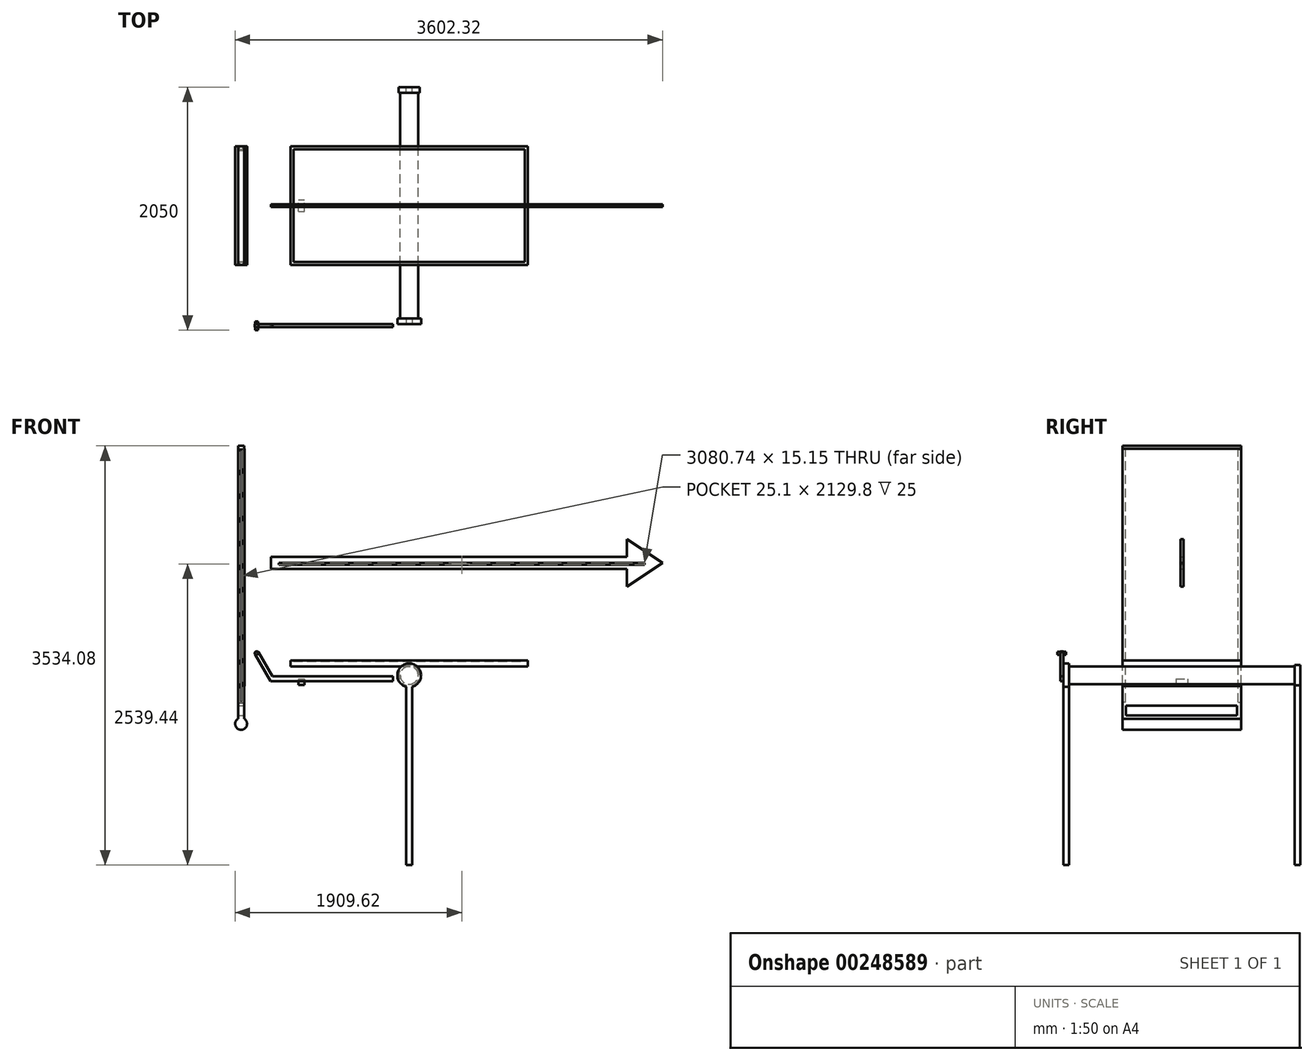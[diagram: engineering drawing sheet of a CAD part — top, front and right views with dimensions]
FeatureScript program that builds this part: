
annotation { "Feature Type Name" : "Feature", "Feature Type Description" : "" }
export const myFeature = defineFeature(function(context is Context, id is Id, definition is map)
    precondition{}
    {
        {
            var Q0;
            Q0=qCreatedBy(makeId("Top.planeOp"),FACE);
            var sketch = newSketch(context, id + "F0", { "sketchPlane" : qUnion([Q0])});
            skLineSegment(sketch, "E0.bottom", {"start": v(-1000, 500) * mm, "end": v(1000, 500) * mm});
            skLineSegment(sketch, "E0.top", {"start": v(-1000, -500) * mm, "end": v(1000, -500) * mm});
            skLineSegment(sketch, "E0.left", {"start": v(-1000, 500) * mm, "end": v(-1000, -500) * mm});
            skLineSegment(sketch, "E0.right", {"start": v(1000, 500) * mm, "end": v(1000, -500) * mm});
            skLineSegment(sketch, "E1", {"start": v(-1000, -500) * mm, "end": v(1000, 500) * mm, "construction": true});
            skSolve(sketch);
        }
        {
            var Q0;
            Q0=makeQuery(id+"F0.imprint","IMPRINT",FACE,{"disambiguationData":[TD([[makeQuery(id+"F0.imprint","IMPRINT",EDGE,{"derivedFrom":sQuery(id+"F0.wireOp",EDGE,"E0.bottom")}),-1.0]])]});
            extrude(context, id + "F1", {"entities" : qUnion([Q0]), "endBound" : BoundingType.SYMMETRIC, "depth" : 50 * mm});
        }
        {
            var Q0;
            Q0=makeQuery(id+"F1.opExtrude","CAP_FACE",FACE,{"disambiguationData":[OSD([sQuery(id+"F0.wireOp",EDGE,"E0.bottom"),sQuery(id+"F0.wireOp",EDGE,"E0.top"),sQuery(id+"F0.wireOp",EDGE,"E0.left"),sQuery(id+"F0.wireOp",EDGE,"E0.right")])],"isStart":false});
            var sketch = newSketch(context, id + "F2", { "sketchPlane" : qUnion([Q0])});
            skLineSegment(sketch, "E2.0", {"start": v(-1000, 500) * mm, "end": v(1000, 500) * mm});
            skLineSegment(sketch, "E3.0", {"start": v(-1000, 500) * mm, "end": v(-1000, -500) * mm});
            skLineSegment(sketch, "E4.0", {"start": v(-1000, -500) * mm, "end": v(1000, -500) * mm});
            skLineSegment(sketch, "E5.0", {"start": v(1000, 500) * mm, "end": v(1000, -500) * mm});
            skLineSegment(sketch, "E6.0", {"start": v(975, 475) * mm, "end": v(975, -475) * mm});
            skLineSegment(sketch, "E6.1", {"start": v(-975, 475) * mm, "end": v(975, 475) * mm});
            skLineSegment(sketch, "E6.2", {"start": v(-975, 475) * mm, "end": v(-975, -475) * mm});
            skLineSegment(sketch, "E6.3", {"start": v(-975, -475) * mm, "end": v(975, -475) * mm});
            skSolve(sketch);
        }
        {
            var Q0;
            Q0=makeQuery(id+"F2.imprint","IMPRINT",FACE,{"disambiguationData":[TD([[makeQuery(id+"F2.imprint","IMPRINT",EDGE,{"derivedFrom":sQuery(id+"F2.wireOp",EDGE,"E2.0")}),-1.0]])]});
            var sketch = newSketch(context, id + "F3", { "sketchPlane" : qUnion([Q0])});
            skSolve(sketch);
        }
        {
            var Q0;
            Q0=qSketchRegion(id+"F3",true);
            var Q1;
            Q1=makeQuery(id+"F2.imprint","IMPRINT",FACE,{"disambiguationData":[TD([[makeQuery(id+"F2.imprint","IMPRINT",EDGE,{"derivedFrom":sQuery(id+"F2.wireOp",EDGE,"E6.0")}),-1.0]])]});
            extrude(context, id + "F4", {"entities" : qUnion([Q0, Q1]), "operationType" : NewBodyOperationType.REMOVE, "oppositeDirection" : true, "depth" : 5 * mm});
        }
        {
            var Q0;
            Q0=qCreatedBy(makeId("Front.planeOp"),FACE);
            var sketch = newSketch(context, id + "F5", { "sketchPlane" : qUnion([Q0])});
            skCircle(sketch, "E7", {"center": v(0, -100) * mm, "radius": 75 * mm});
            skSolve(sketch);
        }
        {
            var Q0;
            Q0=qSketchRegion(id+"F5",true);
            extrude(context, id + "F6", {"entities" : qUnion([Q0]), "operationType" : NewBodyOperationType.ADD, "endBound" : BoundingType.SYMMETRIC, "depth" : 2000 * mm});
        }
        {
            var Q0;
            Q0=makeQuery(id+"F6.opExtrude","CAP_FACE",FACE,{"disambiguationData":[OSD([sQuery(id+"F5.wireOp",EDGE,"E7")])],"isStart":false});
            var sketch = newSketch(context, id + "F7", { "sketchPlane" : qUnion([Q0])});
            skCircle(sketch, "E8.0", {"center": v(0, -100) * mm, "radius": 75 * mm});
            skCircle(sketch, "E9", {"center": v(0, -100) * mm, "radius": 100 * mm});
            skSolve(sketch);
        }
        {
            var Q0;
            Q0=qSketchRegion(id+"F7",true);
            extrude(context, id + "F8", {"entities" : qUnion([Q0]), "operationType" : NewBodyOperationType.ADD, "oppositeDirection" : true, "depth" : 50 * mm});
        }
        {
            var Q0;
            Q0=makeQuery(id+"F8.boolean.opBoolean","MERGE",FACE,{"derivedFrom":[makeQuery(id+"F6.opExtrude","CAP_FACE",FACE,{"disambiguationData":[OSD([sQuery(id+"F5.wireOp",EDGE,"E7")])],"isStart":false}),makeQuery(id+"F8.opExtrude","CAP_FACE",FACE,{"disambiguationData":[OSD([sQuery(id+"F7.wireOp",EDGE,"E8.0"),sQuery(id+"F7.wireOp",EDGE,"E9")])],"isStart":true})]});
            var sketch = newSketch(context, id + "F9", { "sketchPlane" : qUnion([Q0])});
            skLineSegment(sketch, "E10.bottom", {"start": v(-25, -100) * mm, "end": v(25, -100) * mm});
            skLineSegment(sketch, "E10.top", {"start": v(-25, -1700) * mm, "end": v(25, -1700) * mm});
            skLineSegment(sketch, "E10.left", {"start": v(-25, -100) * mm, "end": v(-25, -1700) * mm});
            skLineSegment(sketch, "E10.right", {"start": v(25, -100) * mm, "end": v(25, -1700) * mm});
            skPoint(sketch, "E11", {"position": v(0, -100) * mm});
            skSolve(sketch);
        }
        {
            var Q0;
            Q0=qSketchRegion(id+"F9",true);
            extrude(context, id + "F10", {"entities" : qUnion([Q0]), "operationType" : NewBodyOperationType.ADD, "oppositeDirection" : true, "depth" : 50 * mm});
        }
        {
            var Q0;
            Q0=makeQuery(id+"F6.opExtrude","CAP_FACE",FACE,{"disambiguationData":[OSD([sQuery(id+"F5.wireOp",EDGE,"E7")])],"isStart":true});
            var sketch = newSketch(context, id + "F11", { "sketchPlane" : qUnion([Q0])});
            skCircle(sketch, "E12", {"center": v(0, -100) * mm, "radius": 87.5 * mm});
            skCircle(sketch, "E13.0", {"center": v(0, -100) * mm, "radius": 75 * mm});
            skSolve(sketch);
        }
        {
            var Q0;
            Q0=qSketchRegion(id+"F11",true);
            extrude(context, id + "F12", {"entities" : qUnion([Q0]), "operationType" : NewBodyOperationType.ADD, "oppositeDirection" : true, "depth" : 50 * mm});
        }
        {
            var Q0;
            Q0=makeQuery(id+"F12.boolean.opBoolean","MERGE",FACE,{"derivedFrom":[makeQuery(id+"F6.opExtrude","CAP_FACE",FACE,{"disambiguationData":[OSD([sQuery(id+"F5.wireOp",EDGE,"E7")])],"isStart":true}),makeQuery(id+"F12.opExtrude","CAP_FACE",FACE,{"disambiguationData":[OSD([sQuery(id+"F11.wireOp",EDGE,"E12"),sQuery(id+"F11.wireOp",EDGE,"E13.0")])],"isStart":true})]});
            var sketch = newSketch(context, id + "F13", { "sketchPlane" : qUnion([Q0])});
            skLineSegment(sketch, "E14.0", {"start": v(25, -100) * mm, "end": v(-25, -100) * mm});
            skLineSegment(sketch, "E14.1", {"start": v(25, -1700) * mm, "end": v(-25, -1700) * mm});
            skLineSegment(sketch, "E14.2", {"start": v(25, -100) * mm, "end": v(25, -1700) * mm});
            skLineSegment(sketch, "E14.3", {"start": v(-25, -100) * mm, "end": v(-25, -1700) * mm});
            skPoint(sketch, "E14.4", {"position": v(0, -100) * mm});
            skSolve(sketch);
        }
        {
            var Q0;
            Q0=qSketchRegion(id+"F13",true);
            extrude(context, id + "F14", {"entities" : qUnion([Q0]), "operationType" : NewBodyOperationType.ADD, "oppositeDirection" : true, "depth" : 50 * mm});
        }
        {
            var Q0;
            Q0=qCreatedBy(makeId("Front.planeOp"),FACE);
            var sketch = newSketch(context, id + "F15", { "sketchPlane" : qUnion([Q0])});
            skArc(sketch, "E15", {"start": v(-1441.7, -465.92) * mm, "mid": v(-1416.7, -559.22) * mm, "end": v(-1391.7, -465.92) * mm});
            skLineSegment(sketch, "E16.top", {"start": v(-1441.7, 1834.08) * mm, "end": v(-1391.7, 1834.08) * mm});
            skLineSegment(sketch, "E16.left", {"start": v(-1441.7, -465.92) * mm, "end": v(-1441.7, 1834.08) * mm});
            skLineSegment(sketch, "E16.right", {"start": v(-1391.7, -465.92) * mm, "end": v(-1391.7, 1834.08) * mm});
            skSolve(sketch);
        }
        {
            var Q0;
            Q0=qSketchRegion(id+"F15",true);
            extrude(context, id + "F16", {"entities" : qUnion([Q0]), "endBound" : BoundingType.SYMMETRIC, "depth" : 1000 * mm});
        }
        {
            var Q0;
            Q0=makeQuery(id+"F16.opExtrude","CAP_FACE",FACE,{"disambiguationData":[OSD([sQuery(id+"F15.wireOp",EDGE,"E15"),sQuery(id+"F15.wireOp",EDGE,"E16.top"),sQuery(id+"F15.wireOp",EDGE,"E16.left"),sQuery(id+"F15.wireOp",EDGE,"E16.right")])],"isStart":false});
            var sketch = newSketch(context, id + "F17", { "sketchPlane" : qUnion([Q0])});
            skLineSegment(sketch, "E17.bottom", {"start": v(-1429.3, -326.34) * mm, "end": v(-1404.2, -326.34) * mm});
            skLineSegment(sketch, "E17.left", {"start": v(-1429.3, -326.34) * mm, "end": v(-1429.3, 1803.46) * mm});
            skLineSegment(sketch, "E17.right", {"start": v(-1404.2, -326.34) * mm, "end": v(-1404.2, 1803.46) * mm});
            skLineSegment(sketch, "E18", {"start": v(-1429.3, 1803.46) * mm, "end": v(-1404.2, 1803.46) * mm});
            skSolve(sketch);
        }
        {
            var Q0;
            Q0=qSketchRegion(id+"F17",true);
            extrude(context, id + "F18", {"entities" : qUnion([Q0]), "operationType" : NewBodyOperationType.REMOVE, "oppositeDirection" : true, "depth" : 25 * mm});
        }
        {
            var Q0;
            Q0=makeQuery(id+"F16.opExtrude","SWEPT_BODY",BODY,{"disambiguationData":[OSD([sQuery(id+"F15.wireOp",EDGE,"E15"),sQuery(id+"F15.wireOp",EDGE,"E16.top"),sQuery(id+"F15.wireOp",EDGE,"E16.left"),sQuery(id+"F15.wireOp",EDGE,"E16.right")])]});
            var Q1;
            Q1=makeQuery(id+"F18.boolean.opBoolean","COPY",FACE,{"derivedFrom":makeQuery(id+"F18.opExtrude","SWEPT_FACE",FACE,{"disambiguationData":[OSD([sQuery(id+"F17.wireOp",EDGE,"E17.bottom")])]})});
            var Q2;
            Q2=makeQuery(id+"F18.boolean.opBoolean","COPY",FACE,{"derivedFrom":makeQuery(id+"F18.opExtrude","CAP_FACE",FACE,{"disambiguationData":[OSD([sQuery(id+"F17.wireOp",EDGE,"E17.bottom"),sQuery(id+"F17.wireOp",EDGE,"E17.left"),sQuery(id+"F17.wireOp",EDGE,"E17.right"),sQuery(id+"F17.wireOp",EDGE,"E18")])],"isStart":false})});
            var Q3;
            Q3=makeQuery(id+"F18.boolean.opBoolean","COPY",FACE,{"derivedFrom":makeQuery(id+"F18.opExtrude","SWEPT_FACE",FACE,{"disambiguationData":[OSD([sQuery(id+"F17.wireOp",EDGE,"E17.left")])]})});
            var Q4;
            Q4=makeQuery(id+"F18.boolean.opBoolean","COPY",FACE,{"derivedFrom":makeQuery(id+"F18.opExtrude","SWEPT_FACE",FACE,{"disambiguationData":[OSD([sQuery(id+"F17.wireOp",EDGE,"E17.right")])]})});
            var Q5;
            Q5=makeQuery(id+"F18.boolean.opBoolean","COPY",FACE,{"derivedFrom":makeQuery(id+"F18.opExtrude","SWEPT_FACE",FACE,{"disambiguationData":[OSD([sQuery(id+"F17.wireOp",EDGE,"E18")])]})});
            var Q6;
            Q6=qCreatedBy(makeId("Front.planeOp"),FACE);
            mirror(context, id + "F19", {"entities" : qUnion([Q0]), "faces" : qUnion([Q1, Q2, Q3, Q4, Q5]), "mirrorPlane" : qUnion([Q6]), "patternType" : MirrorType.FACE});
        }
        {
            var Q0;
            Q0=makeQuery(id+"F16.opExtrude","SWEPT_FACE",FACE,{"disambiguationData":[OSD([sQuery(id+"F15.wireOp",EDGE,"E16.right")])]});
            var sketch = newSketch(context, id + "F20", { "sketchPlane" : qUnion([Q0])});
            skLineSegment(sketch, "E19.bottom", {"start": v(-470.62, -438.51) * mm, "end": v(465.7, -438.51) * mm});
            skLineSegment(sketch, "E19.top", {"start": v(-470.62, -355.39) * mm, "end": v(465.7, -355.39) * mm});
            skLineSegment(sketch, "E19.left", {"start": v(-470.62, -438.51) * mm, "end": v(-470.62, -355.39) * mm});
            skLineSegment(sketch, "E19.right", {"start": v(465.7, -438.51) * mm, "end": v(465.7, -355.39) * mm});
            skSolve(sketch);
        }
        {
            var Q0;
            Q0=qSketchRegion(id+"F20",true);
            extrude(context, id + "F21", {"entities" : qUnion([Q0]), "operationType" : NewBodyOperationType.REMOVE, "endBound" : BoundingType.THROUGH_ALL, "oppositeDirection" : true, "depth" : 25 * mm});
        }
        {
            var Q0;
            Q0=makeQuery(id+"F16.opExtrude","SWEPT_FACE",FACE,{"disambiguationData":[OSD([sQuery(id+"F15.wireOp",EDGE,"E16.right")])]});
            var sketch = newSketch(context, id + "F22", { "sketchPlane" : qUnion([Q0])});
            skLineSegment(sketch, "E20.bottom", {"start": v(-500, 1809.08) * mm, "end": v(500, 1809.08) * mm});
            skLineSegment(sketch, "E20.top", {"start": v(-500, -190.92) * mm, "end": v(500, -190.92) * mm});
            skLineSegment(sketch, "E20.left", {"start": v(-500, 1809.08) * mm, "end": v(-500, -190.92) * mm});
            skLineSegment(sketch, "E20.right", {"start": v(500, 1809.08) * mm, "end": v(500, -190.92) * mm});
            skSolve(sketch);
        }
        {
            var Q0;
            Q0=qSketchRegion(id+"F22",true);
            extrude(context, id + "F23", {"entities" : qUnion([Q0]), "operationType" : NewBodyOperationType.ADD, "depth" : 4 * mm});
        }
        {
            var Q0;
            Q0=makeQuery(id+"F7.imprint","IMPRINT",FACE,{"disambiguationData":[TD([[makeQuery(id+"F7.imprint","IMPRINT",EDGE,{"derivedFrom":sQuery(id+"F7.wireOp",EDGE,"E8.0")}),1.0]])]});
            var sketch = newSketch(context, id + "F24", { "sketchPlane" : qUnion([Q0])});
            skLineSegment(sketch, "E21", {"start": v(-136.39, -109.44) * mm, "end": v(-1152.42, -109.44) * mm});
            skLineSegment(sketch, "E22", {"start": v(-1152.42, -109.44) * mm, "end": v(-1270.64, 95.33) * mm});
            skLineSegment(sketch, "E23", {"start": v(-1300.02, 76.23) * mm, "end": v(-1169.74, -149.44) * mm});
            skLineSegment(sketch, "E24", {"start": v(-1169.74, -149.44) * mm, "end": v(-136.39, -149.44) * mm});
            skLineSegment(sketch, "E25", {"start": v(-136.39, -109.44) * mm, "end": v(-136.39, -149.44) * mm});
            skCircle(sketch, "E26", {"center": v(-1284.83, 85) * mm, "radius": 12.5 * mm});
            skArc(sketch, "E27", {"start": v(-1270.64, 95.33) * mm, "mid": v(-1294.4, 99.71) * mm, "end": v(-1300.02, 76.23) * mm});
            skSolve(sketch);
        }
        {
            var Q0;
            Q0=qSketchRegion(id+"F24",true);
            var Q1;
            Q1=qSketchRegion(id+"F26",true);
            extrude(context, id + "F25", {"entities" : qUnion([Q0, Q1]), "depth" : 25 * mm});
        }
        {
            var Q0;
            Q0=makeQuery(id+"F25.opExtrude","CAP_FACE",FACE,{"disambiguationData":[OSD([sQuery(id+"F24.wireOp",EDGE,"E21"),sQuery(id+"F24.wireOp",EDGE,"E22"),sQuery(id+"F24.wireOp",EDGE,"E23"),sQuery(id+"F24.wireOp",EDGE,"E24"),sQuery(id+"F24.wireOp",EDGE,"E25"),sQuery(id+"F24.wireOp",EDGE,"E26"),sQuery(id+"F24.wireOp",EDGE,"E27")])],"isStart":false});
            var sketch = newSketch(context, id + "F26", { "sketchPlane" : qUnion([Q0])});
            skCircle(sketch, "E28.0", {"center": v(-1284.83, 85) * mm, "radius": 12.5 * mm});
            skSolve(sketch);
        }
        {
            var Q0;
            Q0=qSketchRegion(id+"F26",true);
            extrude(context, id + "F27", {"entities" : qUnion([Q0]), "operationType" : NewBodyOperationType.ADD, "oppositeDirection" : true, "depth" : 50 * mm, "hasSecondDirection" : true, "secondDirectionOppositeDirection" : false, "secondDirectionDepth" : 25 * mm});
        }
        {
            var Q0;
            Q0=qCreatedBy(makeId("Front.planeOp"),FACE);
            var sketch = newSketch(context, id + "F28", { "sketchPlane" : qUnion([Q0])});
            skLineSegment(sketch, "E29", {"start": v(-1164.4, 797.02) * mm, "end": v(1835.6, 797.02) * mm});
            skLineSegment(sketch, "E30", {"start": v(1835.6, 797.02) * mm, "end": v(1835.6, 647.02) * mm});
            skLineSegment(sketch, "E31", {"start": v(1835.6, 647.02) * mm, "end": v(2135.6, 847.02) * mm});
            skLineSegment(sketch, "E32", {"start": v(2135.6, 847.02) * mm, "end": v(1835.6, 1047.02) * mm});
            skLineSegment(sketch, "E33", {"start": v(1835.6, 1047.02) * mm, "end": v(1835.6, 897.02) * mm});
            skLineSegment(sketch, "E34", {"start": v(1835.6, 897.02) * mm, "end": v(-1164.4, 897.02) * mm});
            skLineSegment(sketch, "E35", {"start": v(-1164.4, 897.02) * mm, "end": v(-1164.4, 797.02) * mm});
            skSolve(sketch);
        }
        {
            var Q0;
            Q0=qSketchRegion(id+"F28",true);
            extrude(context, id + "F29", {"entities" : qUnion([Q0]), "operationType" : NewBodyOperationType.ADD, "endBound" : BoundingType.SYMMETRIC, "depth" : 25 * mm});
        }
        {
            var Q0;
            Q0=makeQuery(id+"F29.opExtrude","CAP_EDGE",EDGE,{"disambiguationData":[OSD([sQuery(id+"F28.wireOp",EDGE,"E35")])],"isStart":false});
            cPlane(context, id + "F30", {"entities" : qUnion([Q0]), "cplaneType" : CPlaneType.MID_PLANE, "offset" : 150 * mm, "width" : 150 * mm, "height" : 150 * mm});
        }
        {
            var Q0;
            Q0=makeQuery(id+"F29.opExtrude","CAP_FACE",FACE,{"disambiguationData":[OSD([sQuery(id+"F28.wireOp",EDGE,"E29"),sQuery(id+"F28.wireOp",EDGE,"E30"),sQuery(id+"F28.wireOp",EDGE,"E31"),sQuery(id+"F28.wireOp",EDGE,"E32"),sQuery(id+"F28.wireOp",EDGE,"E33"),sQuery(id+"F28.wireOp",EDGE,"E34"),sQuery(id+"F28.wireOp",EDGE,"E35")])],"isStart":false});
            var sketch = newSketch(context, id + "F31", { "sketchPlane" : qUnion([Q0])});
            skLineSegment(sketch, "E36.bottom", {"start": v(1983.28, 847.02) * mm, "end": v(-1097.46, 847.02) * mm});
            skLineSegment(sketch, "E36.top", {"start": v(1983.28, 831.87) * mm, "end": v(-1097.46, 831.87) * mm});
            skLineSegment(sketch, "E36.left", {"start": v(1983.28, 847.02) * mm, "end": v(1983.28, 831.87) * mm});
            skLineSegment(sketch, "E36.right", {"start": v(-1097.46, 847.02) * mm, "end": v(-1097.46, 831.87) * mm});
            skSolve(sketch);
        }
        {
            var Q0;
            Q0=qSketchRegion(id+"F31",true);
            extrude(context, id + "F32", {"entities" : qUnion([Q0]), "operationType" : NewBodyOperationType.REMOVE, "endBound" : BoundingType.THROUGH_ALL, "oppositeDirection" : true, "depth" : 25 * mm});
        }
        {
            var Q0;
            Q0=qCreatedBy(makeId("Front.planeOp"),FACE);
            var sketch = newSketch(context, id + "F33", { "sketchPlane" : qUnion([Q0])});
            skCircle(sketch, "E37", {"center": v(-900.5, 269.22) * mm, "radius": 25 * mm});
            skSolve(sketch);
        }
        {
            var Q0;
            Q0=qSketchRegion(id+"F33",true);
            extrude(context, id + "F34", {"entities" : qUnion([Q0]), "endBound" : BoundingType.SYMMETRIC, "depth" : 100 * mm});
        }
        {
            var Q0;
            Q0=qCreatedBy(makeId("Front.planeOp"),FACE);
            var sketch = newSketch(context, id + "F35", { "sketchPlane" : qUnion([Q0])});
            skLineSegment(sketch, "E38.bottom", {"start": v(-932.76, -131.48) * mm, "end": v(-882.76, -131.48) * mm});
            skLineSegment(sketch, "E38.top", {"start": v(-932.76, -181.48) * mm, "end": v(-882.76, -181.48) * mm});
            skLineSegment(sketch, "E38.left", {"start": v(-932.76, -131.48) * mm, "end": v(-932.76, -181.48) * mm});
            skLineSegment(sketch, "E38.right", {"start": v(-882.76, -131.48) * mm, "end": v(-882.76, -181.48) * mm});
            skSolve(sketch);
        }
        {
            var Q0;
            Q0=qSketchRegion(id+"F35",true);
            extrude(context, id + "F36", {"entities" : qUnion([Q0]), "endBound" : BoundingType.SYMMETRIC, "depth" : 100 * mm});
        }
        {
            var Q0;
            Q0=makeQuery(id+"F34.opExtrude","SWEPT_BODY",BODY,{"disambiguationData":[OSD([sQuery(id+"F33.wireOp",EDGE,"E37")])]});
            deleteBodies(context, id + "F37", {"entities" : qUnion([Q0])});
        }
    });
